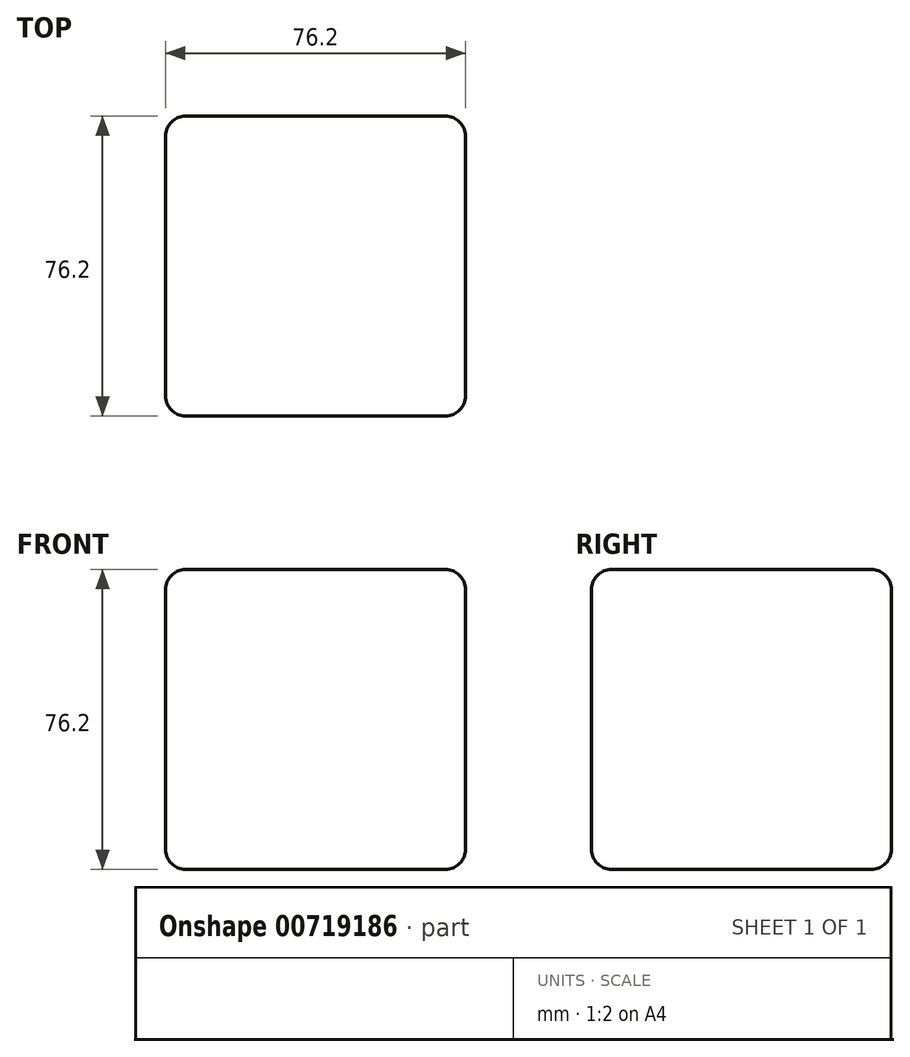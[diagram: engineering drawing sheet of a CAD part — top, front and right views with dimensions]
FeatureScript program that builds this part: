
annotation { "Feature Type Name" : "Feature", "Feature Type Description" : "" }
export const myFeature = defineFeature(function(context is Context, id is Id, definition is map)
    precondition{}
    {
        {
            var Q0;
            Q0=qCreatedBy(makeId("Front.planeOp"),FACE);
            var sketch = newSketch(context, id + "F0", { "sketchPlane" : qUnion([Q0])});
            skLineSegment(sketch, "E0.bottom", {"start": v(38.1, 38.1) * mm, "end": v(-38.1, 38.1) * mm});
            skLineSegment(sketch, "E0.top", {"start": v(38.1, -38.1) * mm, "end": v(-38.1, -38.1) * mm});
            skLineSegment(sketch, "E0.left", {"start": v(38.1, 38.1) * mm, "end": v(38.1, -38.1) * mm});
            skLineSegment(sketch, "E0.right", {"start": v(-38.1, 38.1) * mm, "end": v(-38.1, -38.1) * mm});
            skPoint(sketch, "E0.middle", {"position": v(0, 0) * mm});
            skSolve(sketch);
        }
        {
            var Q0;
            Q0 = qSketchRegion(id + "F0", true);
            extrude(context, id + "F1", {"entities" : qUnion([Q0]), "endBound" : BoundingType.SYMMETRIC, "depth" : 76.2 * mm, "offsetDistance" : 25.4 * mm});
        }
        {
            var Q0;
            Q0=makeQuery(id+"F1.opExtrude","SWEPT_EDGE",EDGE,{"disambiguationData":[OSD([sQuery(id+"F0.wireOp",EDGE,"E0.bottom"),sQuery(id+"F0.wireOp",EDGE,"E0.right")])]});
            var Q1;
            Q1=makeQuery(id+"F1.opExtrude","CAP_EDGE",EDGE,{"disambiguationData":[OSD([sQuery(id+"F0.wireOp",EDGE,"E0.bottom")])],"isStart":false});
            var Q2;
            Q2=makeQuery(id+"F1.opExtrude","SWEPT_FACE",FACE,{"disambiguationData":[OSD([sQuery(id+"F0.wireOp",EDGE,"E0.bottom")])]});
            var Q3;
            Q3=makeQuery(id+"F1.opExtrude","SWEPT_FACE",FACE,{"disambiguationData":[OSD([sQuery(id+"F0.wireOp",EDGE,"E0.right")])]});
            var Q4;
            Q4=makeQuery(id+"F1.opExtrude","CAP_FACE",FACE,{"disambiguationData":[OSD([sQuery(id+"F0.wireOp",EDGE,"E0.bottom"),sQuery(id+"F0.wireOp",EDGE,"E0.top"),sQuery(id+"F0.wireOp",EDGE,"E0.left"),sQuery(id+"F0.wireOp",EDGE,"E0.right")])],"isStart":false});
            var Q5;
            Q5=makeQuery(id+"F1.opExtrude","SWEPT_FACE",FACE,{"disambiguationData":[OSD([sQuery(id+"F0.wireOp",EDGE,"E0.top")])]});
            var Q6;
            Q6=makeQuery(id+"F1.opExtrude","CAP_FACE",FACE,{"disambiguationData":[OSD([sQuery(id+"F0.wireOp",EDGE,"E0.bottom"),sQuery(id+"F0.wireOp",EDGE,"E0.top"),sQuery(id+"F0.wireOp",EDGE,"E0.left"),sQuery(id+"F0.wireOp",EDGE,"E0.right")])],"isStart":true});
            fillet(context, id + "F2", {"entities" : qUnion([Q0, Q1, Q2, Q3, Q4, Q5, Q6]), "radius" : 5.08 * mm, "tangentPropagation" : true, "allowEdgeOverflow" : false});
        }
    });
